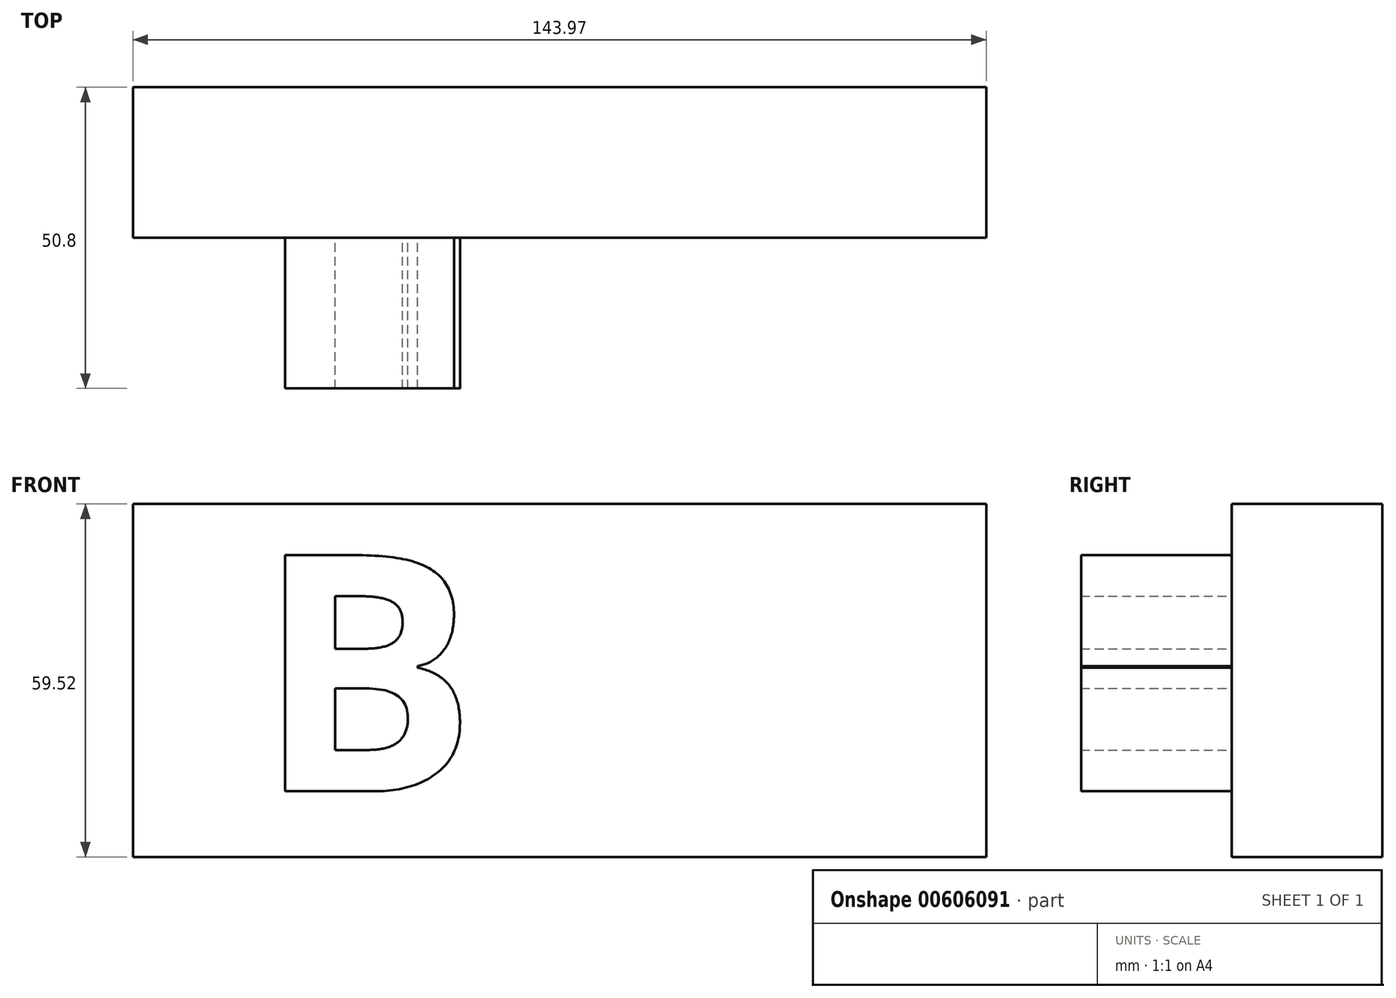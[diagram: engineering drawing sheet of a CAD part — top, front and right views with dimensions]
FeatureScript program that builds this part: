
annotation { "Feature Type Name" : "Feature", "Feature Type Description" : "" }
export const myFeature = defineFeature(function(context is Context, id is Id, definition is map)
    precondition{}
    {
        {
            var Q0;
            Q0=qCreatedBy(makeId("Front.planeOp"),FACE);
            var sketch = newSketch(context, id + "F0", { "sketchPlane" : qUnion([Q0])});
            skLineSegment(sketch, "E0.bottom", {"start": v(-72.45, 48.46) * mm, "end": v(71.52, 48.46) * mm});
            skLineSegment(sketch, "E0.top", {"start": v(-72.45, -11.06) * mm, "end": v(71.52, -11.06) * mm});
            skLineSegment(sketch, "E0.left", {"start": v(-72.45, 48.46) * mm, "end": v(-72.45, -11.06) * mm});
            skLineSegment(sketch, "E0.right", {"start": v(71.52, 48.46) * mm, "end": v(71.52, -11.06) * mm});
            skSolve(sketch);
        }
        {
            var Q0;
            Q0 = qSketchRegion(id + "F0", true);
            extrude(context, id + "F1", {"entities" : qUnion([Q0]), "depth" : 25.4 * mm, "offsetDistance" : 25.4 * mm});
        }
        {
            var Q0;
            Q0=makeQuery(id+"F1.opExtrude","CAP_FACE",FACE,{"disambiguationData":[OSD([sQuery(id+"F0.wireOp",EDGE,"E0.bottom"),sQuery(id+"F0.wireOp",EDGE,"E0.top"),sQuery(id+"F0.wireOp",EDGE,"E0.left"),sQuery(id+"F0.wireOp",EDGE,"E0.right")])],"isStart":false});
            var sketch = newSketch(context, id + "F2", { "sketchPlane" : qUnion([Q0])});
            skText(sketch, "E1", { "text": "B", "fontName": "OpenSans-Bold.ttf"});
            const initialGuessF2  = {"E1": [-0.05181, 0, 1, 0, 0.04016]};
            skSetInitialGuess(sketch, initialGuessF2);
            skSolve(sketch);
        }
        {
            var Q0;
            Q0 = qSketchRegion(id + "F2", true);
            extrude(context, id + "F3", {"entities" : qUnion([Q0]), "operationType" : NewBodyOperationType.ADD, "depth" : 25.4 * mm, "offsetDistance" : 25.4 * mm});
        }
    });
